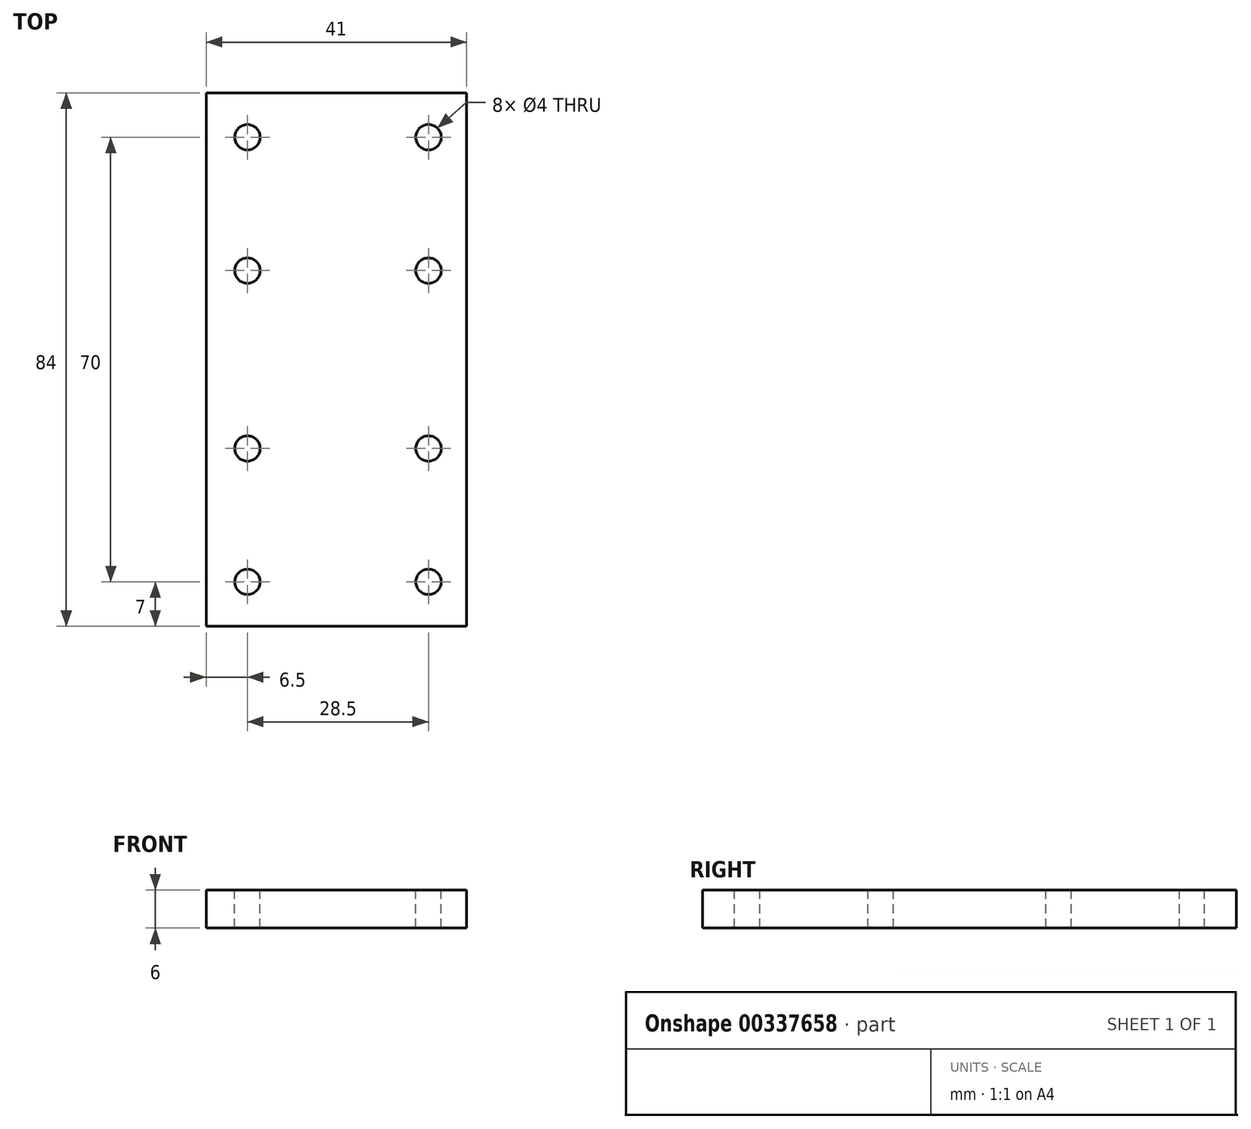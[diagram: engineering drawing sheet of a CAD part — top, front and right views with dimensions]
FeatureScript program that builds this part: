
annotation { "Feature Type Name" : "Feature", "Feature Type Description" : "" }
export const myFeature = defineFeature(function(context is Context, id is Id, definition is map)
    precondition{}
    {
        {
            var Q0;
            Q0=qCreatedBy(makeId("Top.planeOp"),FACE);
            var sketch = newSketch(context, id + "F0", { "sketchPlane" : qUnion([Q0])});
            skLineSegment(sketch, "E0.bottom", {"start": v(20.5, -42) * mm, "end": v(-20.5, -42) * mm});
            skLineSegment(sketch, "E0.top", {"start": v(20.5, 42) * mm, "end": v(-20.5, 42) * mm});
            skLineSegment(sketch, "E0.left", {"start": v(20.5, -42) * mm, "end": v(20.5, 42) * mm});
            skLineSegment(sketch, "E0.right", {"start": v(-20.5, -42) * mm, "end": v(-20.5, 42) * mm});
            skPoint(sketch, "E0.middle", {"position": v(0, 0) * mm});
            skSolve(sketch);
        }
        {
            var Q0;
            Q0=qSketchRegion(id+"F0",true);
            extrude(context, id + "F1", {"entities" : qUnion([Q0]), "depth" : 6 * mm});
        }
        {
            var Q0;
            Q0=makeQuery(id+"F1.opExtrude","CAP_FACE",FACE,{"disambiguationData":[OSD([sQuery(id+"F0.wireOp",EDGE,"E0.bottom"),sQuery(id+"F0.wireOp",EDGE,"E0.top"),sQuery(id+"F0.wireOp",EDGE,"E0.left"),sQuery(id+"F0.wireOp",EDGE,"E0.right")])],"isStart":false});
            var sketch = newSketch(context, id + "F2", { "sketchPlane" : qUnion([Q0])});
            skLineSegment(sketch, "E1", {"start": v(20.5, 0) * mm, "end": v(-20.5, 0) * mm, "construction": true});
            skLineSegment(sketch, "E2", {"start": v(-20.5, 0) * mm, "end": v(-20.5, 0) * mm});
            skLineSegment(sketch, "E3", {"start": v(0, 42) * mm, "end": v(0, -42) * mm, "construction": true});
            skLineSegment(sketch, "E4", {"start": v(0, -42) * mm, "end": v(0, -42) * mm});
            skSolve(sketch);
        }
        {
            var Q0;
            Q0=makeQuery(id+"F2.imprint","IMPRINT",FACE,{"disambiguationData":[TD([[makeQuery(id+"F2.imprint","IMPRINT",EDGE,{"derivedFrom":makeQuery(id+"F1.opExtrude","CAP_EDGE",EDGE,{"disambiguationData":[OSD([sQuery(id+"F0.wireOp",EDGE,"E0.bottom")])],"isStart":false})}),-1.0]])]});
            var sketch = newSketch(context, id + "F3", { "sketchPlane" : qUnion([Q0])});
            skPoint(sketch, "E5", {"position": v(14.5, 35) * mm});
            skPoint(sketch, "E6", {"position": v(14.5, -35) * mm});
            skCircle(sketch, "E7", {"center": v(14.5, -35) * mm, "radius": 2 * mm});
            skCircle(sketch, "E8", {"center": v(14.5, 35) * mm, "radius": 2 * mm});
            skLineSegment(sketch, "E9", {"start": v(14.5, 0) * mm, "end": v(14.5, 14) * mm, "construction": true});
            skLineSegment(sketch, "E10", {"start": v(14.5, 0) * mm, "end": v(14.5, -14) * mm, "construction": true});
            skCircle(sketch, "E11", {"center": v(14.5, 14) * mm, "radius": 2 * mm});
            skCircle(sketch, "E12", {"center": v(14.5, -14) * mm, "radius": 2 * mm});
            skCircle(sketch, "E13", {"center": v(-14, -14) * mm, "radius": 2 * mm});
            skCircle(sketch, "E14", {"center": v(-14, 14) * mm, "radius": 2 * mm});
            skCircle(sketch, "E15", {"center": v(-14, -35) * mm, "radius": 2 * mm});
            skCircle(sketch, "E16", {"center": v(-14, 35) * mm, "radius": 2 * mm});
            skSolve(sketch);
        }
        {
            var Q0;
            Q0=makeQuery(id+"F3.imprint","IMPRINT",FACE,{"disambiguationData":[TD([[makeQuery(id+"F3.imprint","IMPRINT",EDGE,{"derivedFrom":sQuery(id+"F3.wireOp",EDGE,"E14")}),1.0]])]});
            var Q1;
            Q1=makeQuery(id+"F3.imprint","IMPRINT",FACE,{"disambiguationData":[TD([[makeQuery(id+"F3.imprint","IMPRINT",EDGE,{"derivedFrom":sQuery(id+"F3.wireOp",EDGE,"E13")}),1.0]])]});
            var Q2;
            Q2=makeQuery(id+"F3.imprint","IMPRINT",FACE,{"disambiguationData":[TD([[makeQuery(id+"F3.imprint","IMPRINT",EDGE,{"derivedFrom":sQuery(id+"F3.wireOp",EDGE,"0fa5e066-04ea-49e6-b7ea-eb8a54311ce8")}),1.0]])]});
            var Q3;
            Q3=makeQuery(id+"F3.imprint","IMPRINT",FACE,{"disambiguationData":[TD([[makeQuery(id+"F3.imprint","IMPRINT",EDGE,{"derivedFrom":sQuery(id+"F3.wireOp",EDGE,"26436997-3f47-4c4c-a924-85427a2314d3")}),1.0]])]});
            var Q4;
            Q4=makeQuery(id+"F3.imprint","IMPRINT",FACE,{"disambiguationData":[TD([[makeQuery(id+"F3.imprint","IMPRINT",EDGE,{"derivedFrom":sQuery(id+"F3.wireOp",EDGE,"E11")}),1.0]])]});
            var Q5;
            Q5=makeQuery(id+"F3.imprint","IMPRINT",FACE,{"disambiguationData":[TD([[makeQuery(id+"F3.imprint","IMPRINT",EDGE,{"derivedFrom":sQuery(id+"F3.wireOp",EDGE,"E12")}),1.0]])]});
            var Q6;
            Q6=makeQuery(id+"F3.imprint","IMPRINT",FACE,{"disambiguationData":[TD([[makeQuery(id+"F3.imprint","IMPRINT",EDGE,{"derivedFrom":sQuery(id+"F3.wireOp",EDGE,"E7")}),1.0]])]});
            var Q7;
            Q7=makeQuery(id+"F3.imprint","IMPRINT",FACE,{"disambiguationData":[TD([[makeQuery(id+"F3.imprint","IMPRINT",EDGE,{"derivedFrom":sQuery(id+"F3.wireOp",EDGE,"E8")}),1.0]])]});
            var Q8;
            Q8=makeQuery(id+"F3.imprint","IMPRINT",FACE,{"disambiguationData":[TD([[makeQuery(id+"F3.imprint","IMPRINT",EDGE,{"derivedFrom":sQuery(id+"F3.wireOp",EDGE,"29fb6b2e-21ad-41c8-9139-b91c67eb5f50")}),1.0]])]});
            var Q9;
            Q9=makeQuery(id+"F3.imprint","IMPRINT",FACE,{"disambiguationData":[TD([[makeQuery(id+"F3.imprint","IMPRINT",EDGE,{"derivedFrom":sQuery(id+"F3.wireOp",EDGE,"E16")}),1.0]])]});
            var Q10;
            Q10=makeQuery(id+"F3.imprint","IMPRINT",FACE,{"disambiguationData":[TD([[makeQuery(id+"F3.imprint","IMPRINT",EDGE,{"derivedFrom":sQuery(id+"F3.wireOp",EDGE,"f6a00067-0092-4997-b37b-7681e6224854")}),1.0]])]});
            var Q11;
            Q11=makeQuery(id+"F3.imprint","IMPRINT",FACE,{"disambiguationData":[TD([[makeQuery(id+"F3.imprint","IMPRINT",EDGE,{"derivedFrom":sQuery(id+"F3.wireOp",EDGE,"E15")}),1.0]])]});
            extrude(context, id + "F4", {"entities" : qUnion([Q0, Q1, Q2, Q3, Q4, Q5, Q6, Q7, Q8, Q9, Q10, Q11]), "operationType" : NewBodyOperationType.REMOVE, "endBound" : BoundingType.UP_TO_NEXT, "oppositeDirection" : true, "depth" : 25 * mm});
        }
    });
